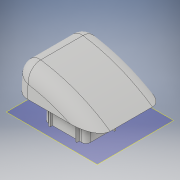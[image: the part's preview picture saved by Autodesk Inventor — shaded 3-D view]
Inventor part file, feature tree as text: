
AUTODESK INVENTOR PART (.ipt)
format: ipt  version: 2017 (Build 210142000, 142)  size: 343,040 bytes
history: native  units: in
note: dims shown in document units (in); Inventor stores cm internally (conversion verified against a paired STEP export)
features: extrude x2, sketch x2, fillet x1, shell x1, plane x1, projected_geometry x1
ambient origin geometry x8: Origin, YZ Plane, XZ Plane, XY Plane, X Axis, Y Axis, Z Axis, Center Point
bodies: Solid1 (feature_tree)
feature tree (8):
  extrude  "Extrusion1"  Depth=6.0in
  fillet  "Fillet1"  Radius=6.0in
  shell  "Shell1"  Thickness=0.64in
  plane  "Work Plane2"
  extrude  "Extrusion2"  Depth=0.4in
  sketch  "Sketch1"  dims[d0=3.04in d2=6.0in d6=6.0in d9=0.64in]
  sketch  "Sketch3"  dims[d10=3.01in d11=0.4in d12=2.55in d13=0.0in d14=0.5in d15=0.07in d36=0.67in d37=1.97in d38=0.68in d39=1.54in d40=0.29in d41=0.15in d42=0.05in d43=0.95in d44=1.94in d45=1.28in d46=0.09in d47=0.05in d48=0.025in d49=0.09in d50=0.05in d51=0.025in d52=0.09in d53=0.05in d54=0.025in d55=0.09in d56=0.025in d57=0.09in d58=0.05in d59=0.025in d60=0.09in d61=0.05in d62=0.025in d63=3.0in d64=0.0in]
  projected_geometry  "Projected Loop4"
